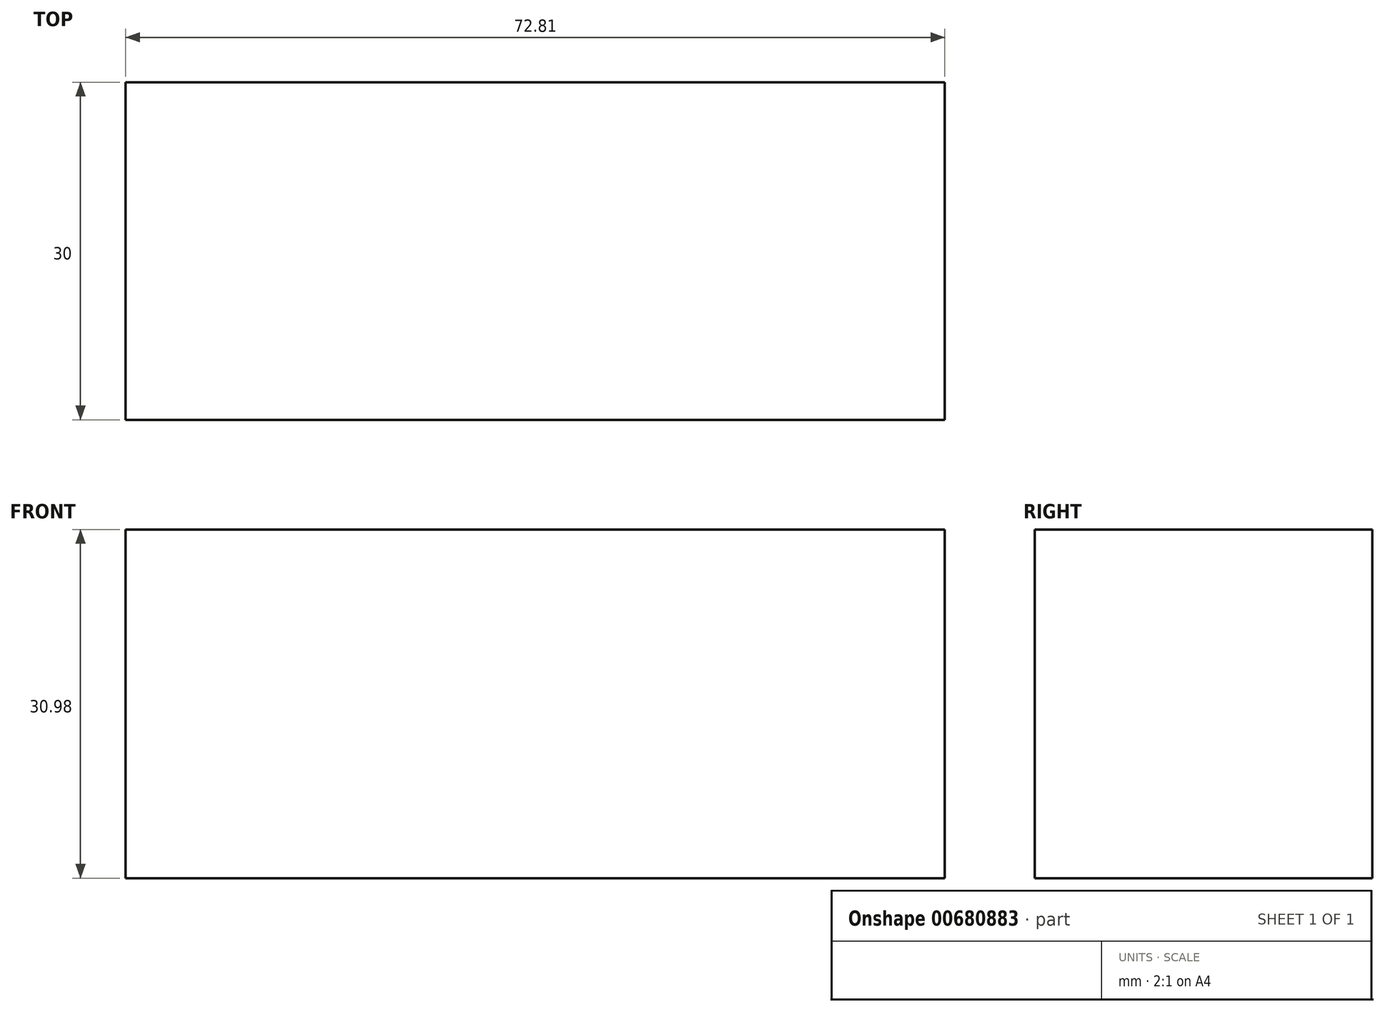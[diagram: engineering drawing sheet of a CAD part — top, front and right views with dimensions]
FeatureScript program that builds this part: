
annotation { "Feature Type Name" : "Feature", "Feature Type Description" : "" }
export const myFeature = defineFeature(function(context is Context, id is Id, definition is map)
    precondition{}
    {
        {
            var Q0;
            Q0=qCreatedBy(makeId("Front.planeOp"),FACE);
            var sketch = newSketch(context, id + "F0", { "sketchPlane" : qUnion([Q0])});
            skLineSegment(sketch, "E0.bottom", {"start": v(0, 0) * mm, "end": v(72.8, 0) * mm});
            skLineSegment(sketch, "E0.top", {"start": v(0, 30.98) * mm, "end": v(72.8, 30.98) * mm});
            skLineSegment(sketch, "E0.left", {"start": v(0, 0) * mm, "end": v(0, 30.98) * mm});
            skLineSegment(sketch, "E0.right", {"start": v(72.8, 0) * mm, "end": v(72.8, 30.98) * mm});
            skSolve(sketch);
        }
        {
            var Q0;
            Q0=makeQuery(id+"F0.imprint","IMPRINT",FACE,{"disambiguationData":[TD([[makeQuery(id+"F0.imprint","IMPRINT",EDGE,{"derivedFrom":sQuery(id+"F0.wireOp",EDGE,"E0.bottom")}),1.0]])]});
            extrude(context, id + "F1", {"entities" : qUnion([Q0]), "endBound" : BoundingType.SYMMETRIC, "depth" : 30 * mm, "offsetDistance" : 25.4 * mm});
        }
    });
